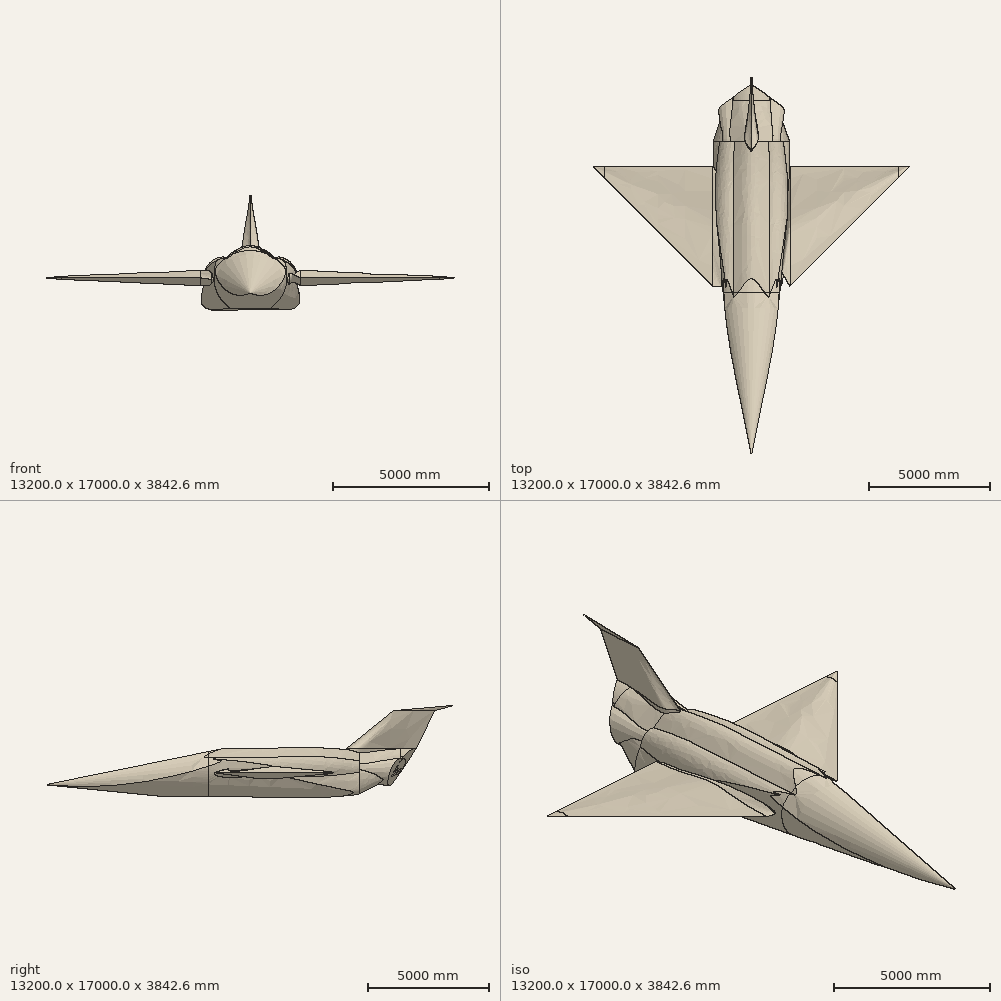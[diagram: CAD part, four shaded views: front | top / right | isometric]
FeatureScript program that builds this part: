
annotation { "Feature Type Name" : "Feature", "Feature Type Description" : "" }
export const myFeature = defineFeature(function(context is Context, id is Id, definition is map)
    precondition{}
    {
        {
            var Q0;
            Q0=qCreatedBy(makeId("Front.planeOp"),FACE);
            cPlane(context, id + "F0", {"entities" : qUnion([Q0]), "cplaneType" : CPlaneType.OFFSET, "offset" : 1750 * mm, "width" : 152.4 * mm, "height" : 152.4 * mm});
        }
        {
            var Q0;
            Q0=qCreatedBy(id+"F0.planeOp",FACE);
            var sketch = newSketch(context, id + "F1", { "sketchPlane" : qUnion([Q0])});
            skLineSegment(sketch, "E0.top", {"start": v(-1394.2, -1000) * mm, "end": v(1394.2, -1000) * mm});
            skPoint(sketch, "E0.middle", {"position": v(0, 0) * mm});
            skFitSpline(sketch, "E1", {"points": [v(-1600, -1000) * mm, v(-848, 530) * mm, v(0, 1000) * mm, v(848, 530) * mm, v(1600, -1000) * mm], "startDerivative": vector(0, 10524.75) * mm, "endDerivative": vector(0, -10524.75) * mm});
            skArc(sketch, "E2", {"start": v(-735.27, 618.52) * mm, "mid": v(-1273.27, 435.52) * mm, "end": v(-1440.68, -107.53) * mm});
            skArc(sketch, "E3.trimOffspring", {"start": v(1440.68, -107.53) * mm, "mid": v(1273.27, 435.52) * mm, "end": v(735.27, 618.52) * mm});
            skFitSpline(sketch, "E4.trimOffspring", {"points": [v(-1600, -1000) * mm, v(-848, 530) * mm, v(0, 1000) * mm, v(848, 530) * mm, v(1600, -1000) * mm], "startDerivative": vector(0, 10524.75) * mm, "endDerivative": vector(0, -10524.75) * mm});
            skFitSpline(sketch, "E5.trimOffspring", {"points": [v(-1600, -1000) * mm, v(-848, 530) * mm, v(0, 1000) * mm, v(848, 530) * mm, v(1600, -1000) * mm], "startDerivative": vector(0, 10524.75) * mm, "endDerivative": vector(0, -10524.75) * mm});
            skArc(sketch, "E6.filletArc", {"start": v(-1593.82, -787.83) * mm, "mid": v(-1539.85, -937.05) * mm, "end": v(-1394.2, -1000) * mm});
            skArc(sketch, "E7.filletArc", {"start": v(1394.2, -1000) * mm, "mid": v(1539.85, -937.05) * mm, "end": v(1593.82, -787.83) * mm});
            skSolve(sketch);
        }
        {
            var Q0;
            Q0=qCreatedBy(makeId("Front.planeOp"),FACE);
            var sketch = newSketch(context, id + "F2", { "sketchPlane" : qUnion([Q0])});
            skLineSegment(sketch, "E8.top", {"start": v(-1394.2, -1000) * mm, "end": v(1394.2, -1000) * mm});
            skPoint(sketch, "E8.middle", {"position": v(0, 0) * mm});
            skFitSpline(sketch, "E9", {"points": [v(-1600, -1000) * mm, v(-848, 530) * mm, v(0, 1000) * mm, v(848, 530) * mm, v(1600, -1000) * mm], "startDerivative": vector(0, 10524.75) * mm, "endDerivative": vector(0, -10524.75) * mm});
            skArc(sketch, "E10", {"start": v(-735.27, 618.52) * mm, "mid": v(-1273.27, 435.52) * mm, "end": v(-1440.68, -107.53) * mm});
            skArc(sketch, "E11.trimOffspring", {"start": v(1440.68, -107.53) * mm, "mid": v(1273.27, 435.52) * mm, "end": v(735.27, 618.52) * mm});
            skFitSpline(sketch, "E12.trimOffspring", {"points": [v(-1600, -1000) * mm, v(-848, 530) * mm, v(0, 1000) * mm, v(848, 530) * mm, v(1600, -1000) * mm], "startDerivative": vector(0, 10524.75) * mm, "endDerivative": vector(0, -10524.75) * mm});
            skFitSpline(sketch, "E13.trimOffspring", {"points": [v(-1600, -1000) * mm, v(-848, 530) * mm, v(0, 1000) * mm, v(848, 530) * mm, v(1600, -1000) * mm], "startDerivative": vector(0, 10524.75) * mm, "endDerivative": vector(0, -10524.75) * mm});
            skArc(sketch, "E14.filletArc", {"start": v(-1593.82, -787.83) * mm, "mid": v(-1539.85, -937.05) * mm, "end": v(-1394.2, -1000) * mm});
            skArc(sketch, "E15.filletArc", {"start": v(1394.2, -1000) * mm, "mid": v(1539.85, -937.05) * mm, "end": v(1593.82, -787.83) * mm});
            skSolve(sketch);
        }
        {
            var Q0;
            Q0=qCreatedBy(makeId("Front.planeOp"),FACE);
            cPlane(context, id + "F3", {"entities" : qUnion([Q0]), "cplaneType" : CPlaneType.OFFSET, "offset" : 3500 * mm, "oppositeDirection" : true, "width" : 150 * mm, "height" : 150 * mm});
        }
        {
            var Q0;
            Q0=qCreatedBy(id+"F3.planeOp",FACE);
            var sketch = newSketch(context, id + "F4", { "sketchPlane" : qUnion([Q0])});
            skLineSegment(sketch, "E16.top", {"start": v(-1394.2, -1000) * mm, "end": v(1394.2, -1000) * mm});
            skPoint(sketch, "E16.middle", {"position": v(0, 0) * mm});
            skFitSpline(sketch, "E17", {"points": [v(-1600, -1000) * mm, v(-848, 530) * mm, v(0, 1000) * mm, v(848, 530) * mm, v(1600, -1000) * mm], "startDerivative": vector(0, 10524.75) * mm, "endDerivative": vector(0, -10524.75) * mm});
            skArc(sketch, "E18", {"start": v(-735.27, 618.52) * mm, "mid": v(-1273.27, 435.52) * mm, "end": v(-1440.68, -107.53) * mm});
            skArc(sketch, "E19.trimOffspring", {"start": v(1440.68, -107.53) * mm, "mid": v(1273.27, 435.52) * mm, "end": v(735.27, 618.52) * mm});
            skFitSpline(sketch, "E20.trimOffspring", {"points": [v(-1600, -1000) * mm, v(-848, 530) * mm, v(0, 1000) * mm, v(848, 530) * mm, v(1600, -1000) * mm], "startDerivative": vector(0, 10524.75) * mm, "endDerivative": vector(0, -10524.75) * mm});
            skFitSpline(sketch, "E21.trimOffspring", {"points": [v(-1600, -1000) * mm, v(-848, 530) * mm, v(0, 1000) * mm, v(848, 530) * mm, v(1600, -1000) * mm], "startDerivative": vector(0, 10524.75) * mm, "endDerivative": vector(0, -10524.75) * mm});
            skArc(sketch, "E22.filletArc", {"start": v(-1593.82, -787.83) * mm, "mid": v(-1539.85, -937.05) * mm, "end": v(-1394.2, -1000) * mm});
            skArc(sketch, "E23.filletArc", {"start": v(1394.2, -1000) * mm, "mid": v(1539.85, -937.05) * mm, "end": v(1593.82, -787.83) * mm});
            skSolve(sketch);
        }
        {
            var Q0;
            Q0=qCreatedBy(makeId("Front.planeOp"),FACE);
            cPlane(context, id + "F5", {"entities" : qUnion([Q0]), "cplaneType" : CPlaneType.OFFSET, "offset" : 4500 * mm, "oppositeDirection" : true, "width" : 150 * mm, "height" : 150 * mm});
        }
        {
            var Q0;
            Q0=qCreatedBy(id+"F5.planeOp",FACE);
            var sketch = newSketch(context, id + "F6", { "sketchPlane" : qUnion([Q0])});
            skLineSegment(sketch, "E24.top", {"start": v(-1413.07, -900) * mm, "end": v(1413.07, -900) * mm});
            skPoint(sketch, "E24.middle", {"position": v(0, 0) * mm});
            skFitSpline(sketch, "E25", {"points": [v(-1600, -900) * mm, v(-784.42, 441.24) * mm, v(0, 900) * mm, v(784.42, 441.24) * mm, v(1600, -900) * mm], "startDerivative": vector(0, 9508.62) * mm, "endDerivative": vector(0, -9508.62) * mm});
            skArc(sketch, "E26", {"start": v(-719.25, 488.69) * mm, "mid": v(-1131.76, 394.84) * mm, "end": v(-1324.66, 18.33) * mm});
            skArc(sketch, "E27.trimOffspring", {"start": v(1324.66, 18.33) * mm, "mid": v(1131.76, 394.84) * mm, "end": v(719.25, 488.69) * mm});
            skFitSpline(sketch, "E28.trimOffspring", {"points": [v(-1600, -900) * mm, v(-784.42, 441.24) * mm, v(0, 900) * mm, v(784.42, 441.24) * mm, v(1600, -900) * mm], "startDerivative": vector(0, 9508.62) * mm, "endDerivative": vector(0, -9508.62) * mm});
            skFitSpline(sketch, "E29.trimOffspring", {"points": [v(-1600, -900) * mm, v(-784.42, 441.24) * mm, v(0, 900) * mm, v(784.42, 441.24) * mm, v(1600, -900) * mm], "startDerivative": vector(0, 9508.62) * mm, "endDerivative": vector(0, -9508.62) * mm});
            skArc(sketch, "E30.filletArc", {"start": v(-1592.48, -705.43) * mm, "mid": v(-1545.4, -842.02) * mm, "end": v(-1413.07, -900) * mm});
            skArc(sketch, "E31.filletArc", {"start": v(1413.07, -900) * mm, "mid": v(1545.4, -842.02) * mm, "end": v(1592.48, -705.43) * mm});
            skLineSegment(sketch, "E32", {"start": v(-719.25, 488.69) * mm, "end": v(-1324.66, 18.33) * mm, "construction": true});
            skLineSegment(sketch, "E33", {"start": v(719.25, 488.69) * mm, "end": v(1324.66, 18.33) * mm, "construction": true});
            skSolve(sketch);
        }
        {
            var Q0;
            Q0=qCreatedBy(makeId("Front.planeOp"),FACE);
            cPlane(context, id + "F7", {"entities" : qUnion([Q0]), "cplaneType" : CPlaneType.OFFSET, "offset" : 6232.05 * mm, "oppositeDirection" : true, "width" : 150 * mm, "height" : 150 * mm});
        }
        {
            var Q0;
            Q0=qCreatedBy(id+"F7.planeOp",FACE);
            var sketch = newSketch(context, id + "F8", { "sketchPlane" : qUnion([Q0])});
            skArc(sketch, "E34", {"start": v(998.61, 52.63) * mm, "mid": v(0, 1000) * mm, "end": v(-998.61, 52.63) * mm});
            skLineSegment(sketch, "E35", {"start": v(0, 0) * mm, "end": v(-948.68, 0) * mm});
            skLineSegment(sketch, "E36", {"start": v(0, 0) * mm, "end": v(948.68, 0) * mm});
            skPoint(sketch, "E37.visualSharp", {"position": v(-1000, 0) * mm});
            skArc(sketch, "E37.filletArc", {"start": v(-998.61, 52.63) * mm, "mid": v(-984.96, 15.59) * mm, "end": v(-948.68, 0) * mm});
            skPoint(sketch, "E38.visualSharp", {"position": v(1000, 0) * mm});
            skArc(sketch, "E38.filletArc", {"start": v(948.68, 0) * mm, "mid": v(984.96, 15.59) * mm, "end": v(998.61, 52.63) * mm});
            skLineSegment(sketch, "E39", {"start": v(0, 1000) * mm, "end": v(0, 675) * mm, "construction": true});
            skPoint(sketch, "E39.endSnap0", {"position": v(0, 1000) * mm});
            skLineSegment(sketch, "E40", {"start": v(0, 675) * mm, "end": v(737.82, 675) * mm, "construction": true});
            skLineSegment(sketch, "E41", {"start": v(0, 675) * mm, "end": v(-737.82, 675) * mm, "construction": true});
            skSolve(sketch);
        }
        {
            var Q0;
            Q0=qSketchRegion(id+"F1",true);
            var Q1;
            Q1=qSketchRegion(id+"F2",true);
            var Q2;
            Q2=qSketchRegion(id+"F4",true);
            var Q3;
            Q3=qSketchRegion(id+"F6",true);
            loft(context, id + "F9", {"sheetProfilesArray" : [{ "sheetProfileEntities" : qUnion([Q0]) }, { "sheetProfileEntities" : qUnion([Q1]) }, { "sheetProfileEntities" : qUnion([Q2]) }, { "sheetProfileEntities" : qUnion([Q3]) }]});
        }
        {
            var Q0;
            Q0=sQuery(id+"F6.wireOp",EDGE,"E32");
            var Q1;
            Q1=sQuery(id+"F8.wireOp",VERTEX,"E41.end");
            cPlane(context, id + "F10", {"entities" : qUnion([Q0, Q1]), "cplaneType" : CPlaneType.LINE_ANGLE, "offset" : 25 * mm, "angle" : 0 * degree, "width" : 150 * mm, "height" : 150 * mm});
        }
        {
            var Q0;
            Q0=qCreatedBy(id+"F10.planeOp",FACE);
            var sketch = newSketch(context, id + "F11", { "sketchPlane" : qUnion([Q0])});
            skLineSegment(sketch, "E42", {"start": v(-589.34, -4526.34) * mm, "end": v(-612.8, -6268.32) * mm});
            skLineSegment(sketch, "E43", {"start": v(-1354.08, -4472.19) * mm, "end": v(-612.8, -6268.32) * mm});
            skSolve(sketch);
        }
        {
            var Q0;
            Q0=sQuery(id+"F6.wireOp",EDGE,"E33");
            var Q1;
            Q1=sQuery(id+"F8.wireOp",VERTEX,"E40.end");
            cPlane(context, id + "F12", {"entities" : qUnion([Q0, Q1]), "cplaneType" : CPlaneType.LINE_ANGLE, "offset" : 25 * mm, "angle" : 0 * degree, "width" : 150 * mm, "height" : 150 * mm});
        }
        {
            var Q0;
            Q0=qCreatedBy(id+"F12.planeOp",FACE);
            var sketch = newSketch(context, id + "F13", { "sketchPlane" : qUnion([Q0])});
            skLineSegment(sketch, "E44", {"start": v(589.34, 4526.34) * mm, "end": v(612.8, 6268.32) * mm});
            skLineSegment(sketch, "E45", {"start": v(1354.08, 4472.19) * mm, "end": v(612.8, 6268.32) * mm});
            skSolve(sketch);
        }
        {
            var Q1;
            Q1=makeQuery(id+"F6.imprint","IMPRINT",FACE,{"disambiguationData":[TD([[makeQuery(id+"F6.imprint","IMPRINT",EDGE,{"derivedFrom":sQuery(id+"F6.wireOp",EDGE,"E24.top")}),1.0]])]});
            var Q2;
            Q2=makeQuery(id+"F8.imprint","IMPRINT",FACE,{"disambiguationData":[TD([[makeQuery(id+"F8.imprint","IMPRINT",EDGE,{"derivedFrom":sQuery(id+"F8.wireOp",EDGE,"E34")}),1.0]])]});
            var Q3;
            Q3=sQuery(id+"F11.wireOp",EDGE,"E42");
            var Q4;
            Q4=sQuery(id+"F13.wireOp",EDGE,"E44");
            loft(context, id + "F14", {"operationType" : NewBodyOperationType.ADD, "addGuides" : true, "sheetProfilesArray" : [{ "sheetProfileEntities" : qUnion([Q1]) }, { "sheetProfileEntities" : qUnion([Q2]) }], "guidesArray" : [{ "guideEntities" : qUnion([Q3]), "guideDerivativeType" : LoftGuideDerivativeType.DEFAULT, "guideDerivativeMagnitude" : 1 }, { "guideEntities" : qUnion([Q4]), "guideDerivativeType" : LoftGuideDerivativeType.DEFAULT, "guideDerivativeMagnitude" : 1 }]});
        }
        {
            var Q0;
            Q0=makeQuery(id+"F14.opLoft","CAP_FACE",FACE,{"disambiguationData":[OSD([makeQuery(id+"F8.imprint","IMPRINT",FACE,{"disambiguationData":[TD([[makeQuery(id+"F8.imprint","IMPRINT",EDGE,{"derivedFrom":sQuery(id+"F8.wireOp",EDGE,"E34")}),1.0]])]})])],"isStart":true});
            extrude(context, id + "F15", {"entities" : qUnion([Q0]), "operationType" : NewBodyOperationType.ADD, "depth" : 649.4 * mm});
        }
        {
            var Q0;
            Q0=qCreatedBy(makeId("Right.planeOp"),FACE);
            var sketch = newSketch(context, id + "F16", { "sketchPlane" : qUnion([Q0])});
            skLineSegment(sketch, "E46", {"start": v(0, 0) * mm, "end": v(4500, 0) * mm});
            skLineSegment(sketch, "E47", {"start": v(4500, 0) * mm, "end": v(6232.05, 0) * mm});
            skLineSegment(sketch, "E48", {"start": v(4500, 0) * mm, "end": v(4500, 1000) * mm});
            skLineSegment(sketch, "E49", {"start": v(4500, 1000) * mm, "end": v(6881.46, 1000) * mm});
            skLineSegment(sketch, "E50", {"start": v(6881.46, 1000) * mm, "end": v(6881.46, -1000) * mm});
            skLineSegment(sketch, "E51", {"start": v(6881.46, 1000) * mm, "end": v(6232.05, 0) * mm});
            skLineSegment(sketch, "E52", {"start": v(6232.05, 0) * mm, "end": v(5582.64, -1000) * mm});
            skLineSegment(sketch, "E53", {"start": v(5582.64, -1000) * mm, "end": v(6881.46, -1000) * mm});
            skSolve(sketch);
        }
        {
            var Q0;
            Q0=makeQuery(id+"F16.imprint","IMPRINT",FACE,{"disambiguationData":[TD([[makeQuery(id+"F16.imprint","IMPRINT",EDGE,{"derivedFrom":sQuery(id+"F16.wireOp",EDGE,"E50")}),-1.0]])]});
            var Q1;
            Q1=sQuery(id+"F16.wireOp",EDGE,"E49");
            revolve(context, id + "F17", {"operationType" : NewBodyOperationType.REMOVE, "entities" : qUnion([Q0]), "axis" : qUnion([Q1]), "revolveType" : RevolveType.SYMMETRIC, "oppositeDirection" : true, "angle" : 182 * degree});
        }
        {
            var Q0;
            Q0=makeQuery(id+"F9.opLoft","CAP_FACE",FACE,{"disambiguationData":[OSD([makeQuery(id+"F1.imprint","IMPRINT",FACE,{"disambiguationData":[TD([[makeQuery(id+"F1.imprint","IMPRINT",EDGE,{"derivedFrom":sQuery(id+"F1.wireOp",EDGE,"E0.top")}),1.0]])]})])],"isStart":true});
            extrude(context, id + "F18", {"entities" : qUnion([Q0]), "depth" : 6750 * mm});
        }
        {
            var Q0;
            Q0=qCreatedBy(makeId("Right.planeOp"),FACE);
            var sketch = newSketch(context, id + "F19", { "sketchPlane" : qUnion([Q0])});
            skLineSegment(sketch, "E54", {"start": v(0, 0) * mm, "end": v(-3500, 0) * mm});
            skLineSegment(sketch, "E55", {"start": v(-3500, 0) * mm, "end": v(-3500, -1000) * mm});
            skLineSegment(sketch, "E56", {"start": v(-3500, -1000) * mm, "end": v(-8500, -1000) * mm});
            skLineSegment(sketch, "E57", {"start": v(-8500, -1000) * mm, "end": v(-8500, -499.31) * mm});
            skLineSegment(sketch, "E58", {"start": v(-1151.4, 0) * mm, "end": v(-1151.4, 1000) * mm});
            skLineSegment(sketch, "E59", {"start": v(-1151.4, 1000) * mm, "end": v(-8500, -499.31) * mm});
            skLineSegment(sketch, "E60", {"start": v(-8500, -499.31) * mm, "end": v(-3500, -1000) * mm});
            skLineSegment(sketch, "E61", {"start": v(-1151.4, 1000) * mm, "end": v(-8500, 1000) * mm});
            skLineSegment(sketch, "E62", {"start": v(-8500, 1000) * mm, "end": v(-8500, -499.31) * mm});
            skLineSegment(sketch, "E63", {"start": v(-8500, -1000) * mm, "end": v(-8500, -1980) * mm});
            skLineSegment(sketch, "E64", {"start": v(-3500, -1000) * mm, "end": v(6286.5, -1980) * mm});
            skLineSegment(sketch, "E65", {"start": v(6286.5, -1980) * mm, "end": v(-8500, -1980) * mm});
            skLineSegment(sketch, "E66", {"start": v(-8500, -499.31) * mm, "end": v(-3500, -499.31) * mm});
            skSolve(sketch);
        }
        {
            var Q0;
            Q0=makeQuery(id+"F19.imprint","IMPRINT",FACE,{"disambiguationData":[TD([[makeQuery(id+"F19.imprint","IMPRINT",EDGE,{"derivedFrom":sQuery(id+"F19.wireOp",EDGE,"E59")}),-1.0]])]});
            var Q1;
            Q1=sQuery(id+"F19.wireOp",EDGE,"E66");
            revolve(context, id + "F20", {"operationType" : NewBodyOperationType.REMOVE, "entities" : qUnion([Q0]), "axis" : qUnion([Q1]), "revolveType" : RevolveType.SYMMETRIC, "oppositeDirection" : true, "angle" : 250 * degree});
        }
        {
            var Q0;
            Q0=makeQuery(id+"F19.imprint","IMPRINT",FACE,{"disambiguationData":[TD([[makeQuery(id+"F19.imprint","IMPRINT",EDGE,{"derivedFrom":sQuery(id+"F19.wireOp",EDGE,"E56")}),-1.0]])]});
            var Q1;
            Q1=makeQuery(id+"F19.imprint","IMPRINT",FACE,{"disambiguationData":[TD([[makeQuery(id+"F19.imprint","IMPRINT",EDGE,{"derivedFrom":sQuery(id+"F19.wireOp",EDGE,"E56")}),1.0]])]});
            var Q2;
            Q2=sQuery(id+"F19.wireOp",EDGE,"E54");
            revolve(context, id + "F21", {"operationType" : NewBodyOperationType.REMOVE, "entities" : qUnion([Q0, Q1]), "axis" : qUnion([Q2]), "revolveType" : RevolveType.SYMMETRIC, "oppositeDirection" : true, "angle" : 240 * degree});
        }
        {
            var Q0;
            Q0=qCreatedBy(makeId("Front.planeOp"),FACE);
            cPlane(context, id + "F22", {"entities" : qUnion([Q0]), "cplaneType" : CPlaneType.OFFSET, "offset" : 3500 * mm, "oppositeDirection" : true, "width" : 150 * mm, "height" : 150 * mm});
        }
        {
            var Q0;
            Q0=qCreatedBy(id+"F22.planeOp",FACE);
            var sketch = newSketch(context, id + "F23", { "sketchPlane" : qUnion([Q0])});
            skCircle(sketch, "E67", {"center": v(-825, 0) * mm, "radius": 600 * mm});
            skCircle(sketch, "E68", {"center": v(825, 0) * mm, "radius": 600 * mm});
            skSolve(sketch);
        }
        {
            var Q0;
            Q0=qCreatedBy(makeId("Front.planeOp"),FACE);
            cPlane(context, id + "F24", {"entities" : qUnion([Q0]), "cplaneType" : CPlaneType.OFFSET, "offset" : 4500 * mm, "oppositeDirection" : true, "width" : 150 * mm, "height" : 150 * mm});
        }
        {
            var Q0;
            Q0=qCreatedBy(id+"F24.planeOp",FACE);
            var sketch = newSketch(context, id + "F25", { "sketchPlane" : qUnion([Q0])});
            skCircle(sketch, "E69", {"center": v(-825, 0) * mm, "radius": 400 * mm});
            skCircle(sketch, "E70", {"center": v(825, 0) * mm, "radius": 400 * mm});
            skSolve(sketch);
        }
        {
            var Q0;
            Q0=qCreatedBy(makeId("Front.planeOp"),FACE);
            cPlane(context, id + "F26", {"entities" : qUnion([Q0]), "cplaneType" : CPlaneType.OFFSET, "offset" : 6232.05 * mm, "oppositeDirection" : true, "width" : 150 * mm, "height" : 150 * mm});
        }
        {
            var Q0;
            Q0=qCreatedBy(id+"F26.planeOp",FACE);
            var sketch = newSketch(context, id + "F27", { "sketchPlane" : qUnion([Q0])});
            skCircle(sketch, "E71", {"center": v(-825, 0) * mm, "radius": 600 * mm});
            skCircle(sketch, "E72", {"center": v(825, 0) * mm, "radius": 600 * mm});
            skSolve(sketch);
        }
        {
            var Q0;
            Q0=qCreatedBy(makeId("Front.planeOp"),FACE);
            cPlane(context, id + "F28", {"entities" : qUnion([Q0]), "cplaneType" : CPlaneType.OFFSET, "offset" : 6732.05 * mm, "oppositeDirection" : true, "width" : 150 * mm, "height" : 150 * mm});
        }
        {
            var Q0;
            Q0=qCreatedBy(id+"F28.planeOp",FACE);
            var sketch = newSketch(context, id + "F29", { "sketchPlane" : qUnion([Q0])});
            skCircle(sketch, "E73", {"center": v(-825, 0) * mm, "radius": 600 * mm});
            skCircle(sketch, "E74", {"center": v(825, 0) * mm, "radius": 600 * mm});
            skSolve(sketch);
        }
        {
            var Q0;
            Q0=makeQuery(id+"F23.imprint","IMPRINT",FACE,{"disambiguationData":[TD([[makeQuery(id+"F23.imprint","IMPRINT",EDGE,{"derivedFrom":sQuery(id+"F23.wireOp",EDGE,"E67")}),1.0]])]});
            var Q1;
            Q1=makeQuery(id+"F25.imprint","IMPRINT",FACE,{"disambiguationData":[TD([[makeQuery(id+"F25.imprint","IMPRINT",EDGE,{"derivedFrom":sQuery(id+"F25.wireOp",EDGE,"E69")}),1.0]])]});
            var Q2;
            Q2=makeQuery(id+"F27.imprint","IMPRINT",FACE,{"disambiguationData":[TD([[makeQuery(id+"F27.imprint","IMPRINT",EDGE,{"derivedFrom":sQuery(id+"F27.wireOp",EDGE,"E71")}),1.0]])]});
            var Q3;
            Q3=makeQuery(id+"F29.imprint","IMPRINT",FACE,{"disambiguationData":[TD([[makeQuery(id+"F29.imprint","IMPRINT",EDGE,{"derivedFrom":sQuery(id+"F29.wireOp",EDGE,"E73")}),1.0]])]});
            loft(context, id + "F30", {"sheetProfilesArray" : [{ "sheetProfileEntities" : qUnion([Q0]) }, { "sheetProfileEntities" : qUnion([Q1]) }, { "sheetProfileEntities" : qUnion([Q2]) }, { "sheetProfileEntities" : qUnion([Q3]) }]});
        }
        {
            var Q0;
            Q0=makeQuery(id+"F23.imprint","IMPRINT",FACE,{"disambiguationData":[TD([[makeQuery(id+"F23.imprint","IMPRINT",EDGE,{"derivedFrom":sQuery(id+"F23.wireOp",EDGE,"E68")}),1.0]])]});
            var Q1;
            Q1=makeQuery(id+"F25.imprint","IMPRINT",FACE,{"disambiguationData":[TD([[makeQuery(id+"F25.imprint","IMPRINT",EDGE,{"derivedFrom":sQuery(id+"F25.wireOp",EDGE,"E70")}),1.0]])]});
            var Q2;
            Q2=makeQuery(id+"F27.imprint","IMPRINT",FACE,{"disambiguationData":[TD([[makeQuery(id+"F27.imprint","IMPRINT",EDGE,{"derivedFrom":sQuery(id+"F27.wireOp",EDGE,"E72")}),1.0]])]});
            var Q3;
            Q3=makeQuery(id+"F29.imprint","IMPRINT",FACE,{"disambiguationData":[TD([[makeQuery(id+"F29.imprint","IMPRINT",EDGE,{"derivedFrom":sQuery(id+"F29.wireOp",EDGE,"E74")}),1.0]])]});
            loft(context, id + "F31", {"sheetProfilesArray" : [{ "sheetProfileEntities" : qUnion([Q0]) }, { "sheetProfileEntities" : qUnion([Q1]) }, { "sheetProfileEntities" : qUnion([Q2]) }, { "sheetProfileEntities" : qUnion([Q3]) }]});
        }
        {
            var Q0;
            Q0=qCreatedBy(makeId("Top.planeOp"),FACE);
            var sketch = newSketch(context, id + "F32", { "sketchPlane" : qUnion([Q0])});
            skLineSegment(sketch, "E75", {"start": v(0, 0) * mm, "end": v(0, 1000) * mm});
            skLineSegment(sketch, "E76", {"start": v(0, 1000) * mm, "end": v(-1600, 1000) * mm});
            skLineSegment(sketch, "E77", {"start": v(-1600, 1000) * mm, "end": v(-1600, -1500) * mm});
            skLineSegment(sketch, "E78", {"start": v(-1600, 1000) * mm, "end": v(-1600, 3500) * mm});
            skLineSegment(sketch, "E79", {"start": v(-1600, 3500) * mm, "end": v(-6100, 3500) * mm});
            skLineSegment(sketch, "E80", {"start": v(-6100, 3500) * mm, "end": v(-6600, 3500) * mm});
            skLineSegment(sketch, "E81", {"start": v(-6100, 3500) * mm, "end": v(-6100, 3000) * mm});
            skLineSegment(sketch, "E82", {"start": v(-1600, -1500) * mm, "end": v(-6100, 3000) * mm});
            skLineSegment(sketch, "E83", {"start": v(0, 1000) * mm, "end": v(1600, 1000) * mm});
            skLineSegment(sketch, "E84", {"start": v(1600, 1000) * mm, "end": v(1600, -1500) * mm});
            skLineSegment(sketch, "E85", {"start": v(1600, 1000) * mm, "end": v(1600, 3500) * mm});
            skLineSegment(sketch, "E86", {"start": v(1600, 3500) * mm, "end": v(6100, 3500) * mm});
            skLineSegment(sketch, "E87", {"start": v(6100, 3500) * mm, "end": v(6600, 3500) * mm});
            skLineSegment(sketch, "E88", {"start": v(6100, 3500) * mm, "end": v(6100, 3000) * mm});
            skLineSegment(sketch, "E89", {"start": v(1600, -1500) * mm, "end": v(6100, 3000) * mm});
            skSolve(sketch);
        }
        {
            var Q0;
            Q0=qCreatedBy(makeId("Right.planeOp"),FACE);
            var sketch = newSketch(context, id + "F33", { "sketchPlane" : qUnion([Q0])});
            skFitSpline(sketch, "E90", {"points": [v(-1500, -50) * mm, v(0, 250) * mm, v(3000, -50) * mm, v(0, -250) * mm, v(-1500, -50) * mm]});
            skSolve(sketch);
        }
        {
            var Q0;
            Q0=qCreatedBy(makeId("Right.planeOp"),FACE);
            cPlane(context, id + "F34", {"entities" : qUnion([Q0]), "cplaneType" : CPlaneType.OFFSET, "offset" : 1600 * mm, "oppositeDirection" : true, "width" : 150 * mm, "height" : 150 * mm});
        }
        {
            var Q0;
            Q0=qCreatedBy(id+"F34.planeOp",FACE);
            var sketch = newSketch(context, id + "F35", { "sketchPlane" : qUnion([Q0])});
            skFitSpline(sketch, "E91", {"points": [v(-1500, 0) * mm, v(1000, 250) * mm, v(3500, 0) * mm], "startDerivative": vector(7500, 0) * mm, "endDerivative": vector(7500, 0) * mm});
            skFitSpline(sketch, "E92", {"points": [v(-1500, 0) * mm, v(1000, -250) * mm, v(3500, 0) * mm], "startDerivative": vector(5000, -750) * mm, "endDerivative": vector(7500, 0) * mm});
            skSolve(sketch);
        }
        {
            var Q0;
            Q0=qCreatedBy(makeId("Right.planeOp"),FACE);
            cPlane(context, id + "F36", {"entities" : qUnion([Q0]), "cplaneType" : CPlaneType.OFFSET, "offset" : 1600 * mm, "width" : 150 * mm, "height" : 150 * mm});
        }
        {
            var Q0;
            Q0=qCreatedBy(id+"F36.planeOp",FACE);
            var sketch = newSketch(context, id + "F37", { "sketchPlane" : qUnion([Q0])});
            skFitSpline(sketch, "E93", {"points": [v(-1500, 0) * mm, v(1000, 250) * mm, v(3500, 0) * mm], "startDerivative": vector(7500, 0) * mm, "endDerivative": vector(7500, 0) * mm});
            skFitSpline(sketch, "E94", {"points": [v(-1500, 0) * mm, v(1000, -250) * mm, v(3500, 0) * mm], "startDerivative": vector(5000, -750) * mm, "endDerivative": vector(7500, 0) * mm});
            skSolve(sketch);
        }
        {
            var Q0;
            Q0=qCreatedBy(makeId("Right.planeOp"),FACE);
            cPlane(context, id + "F38", {"entities" : qUnion([Q0]), "cplaneType" : CPlaneType.OFFSET, "offset" : 6100 * mm, "oppositeDirection" : true, "width" : 150 * mm, "height" : 150 * mm});
        }
        {
            var Q0;
            Q0=qCreatedBy(id+"F38.planeOp",FACE);
            var sketch = newSketch(context, id + "F39", { "sketchPlane" : qUnion([Q0])});
            skFitSpline(sketch, "E95", {"points": [v(3000, 0) * mm, v(3250, 50) * mm, v(3500, 0) * mm], "startDerivative": vector(750, 0) * mm, "endDerivative": vector(750, 0) * mm});
            skFitSpline(sketch, "E96", {"points": [v(3000, 0) * mm, v(3250, -50) * mm, v(3500, 0) * mm], "startDerivative": vector(500, -150) * mm, "endDerivative": vector(750, 0) * mm});
            skSolve(sketch);
        }
        {
            var Q0;
            Q0=qCreatedBy(makeId("Right.planeOp"),FACE);
            cPlane(context, id + "F40", {"entities" : qUnion([Q0]), "cplaneType" : CPlaneType.OFFSET, "offset" : 6100 * mm, "width" : 150 * mm, "height" : 150 * mm});
        }
        {
            var Q0;
            Q0=qCreatedBy(id+"F40.planeOp",FACE);
            var sketch = newSketch(context, id + "F41", { "sketchPlane" : qUnion([Q0])});
            skFitSpline(sketch, "E97", {"points": [v(3000, 0) * mm, v(3250, 50) * mm, v(3500, 0) * mm], "startDerivative": vector(850.99, 0) * mm, "endDerivative": vector(750, 0) * mm});
            skFitSpline(sketch, "E98", {"points": [v(3000, 0) * mm, v(3250, -50) * mm, v(3500, 0) * mm], "startDerivative": vector(500, -150) * mm, "endDerivative": vector(750, 0) * mm});
            skSolve(sketch);
        }
        {
            var Q0;
            Q0=qSketchRegion(id+"F33",true);
            extrude(context, id + "F42", {"entities" : qUnion([Q0]), "endBound" : BoundingType.SYMMETRIC, "depth" : 2500 * mm});
        }
        {
            var Q1;
            Q1=makeQuery(id+"F42.opExtrude","CAP_FACE",FACE,{"disambiguationData":[OSD([sQuery(id+"F33.wireOp",EDGE,"E90")])],"isStart":true});
            var Q2;
            {var subQ0=sQuery(id+"F35.wireOp",EDGE,"E91");Q2=makeQuery(id+"F35.imprint","IMPRINT",FACE,{"disambiguationData":[TD([[makeQuery(id+"F35.imprint","IMPRINT",EDGE,{"derivedFrom":subQ0}),-1.0]])]});}
            loft(context, id + "F43", {"operationType" : NewBodyOperationType.ADD, "sheetProfilesArray" : [{ "sheetProfileEntities" : qUnion([Q1]) }, { "sheetProfileEntities" : qUnion([Q2]) }]});
        }
        {
            var Q1;
            Q1=makeQuery(id+"F42.opExtrude","CAP_FACE",FACE,{"disambiguationData":[OSD([sQuery(id+"F33.wireOp",EDGE,"E90")])],"isStart":false});
            var Q2;
            {var subQ0=sQuery(id+"F37.wireOp",EDGE,"E93");Q2=makeQuery(id+"F37.imprint","IMPRINT",FACE,{"disambiguationData":[TD([[makeQuery(id+"F37.imprint","IMPRINT",EDGE,{"derivedFrom":subQ0}),-1.0]])]});}
            loft(context, id + "F44", {"operationType" : NewBodyOperationType.ADD, "sheetProfilesArray" : [{ "sheetProfileEntities" : qUnion([Q1]) }, { "sheetProfileEntities" : qUnion([Q2]) }]});
        }
        {
            var Q1;
            {var subQ0=sQuery(id+"F35.wireOp",EDGE,"E91");Q1=makeQuery(id+"F43.opLoft","CAP_FACE",FACE,{"disambiguationData":[OSD([makeQuery(id+"F35.imprint","IMPRINT",FACE,{"disambiguationData":[TD([[makeQuery(id+"F35.imprint","IMPRINT",EDGE,{"derivedFrom":subQ0}),-1.0]])]})])],"isStart":true});}
            var Q2;
            {var subQ0=sQuery(id+"F39.wireOp",EDGE,"E95");Q2=makeQuery(id+"F39.imprint","IMPRINT",FACE,{"disambiguationData":[TD([[makeQuery(id+"F39.imprint","IMPRINT",EDGE,{"derivedFrom":subQ0}),-1.0]])]});}
            loft(context, id + "F45", {"operationType" : NewBodyOperationType.ADD, "sheetProfilesArray" : [{ "sheetProfileEntities" : qUnion([Q1]) }, { "sheetProfileEntities" : qUnion([Q2]) }]});
        }
        {
            var Q1;
            {var subQ0=sQuery(id+"F37.wireOp",EDGE,"E93");Q1=makeQuery(id+"F44.opLoft","CAP_FACE",FACE,{"disambiguationData":[OSD([makeQuery(id+"F37.imprint","IMPRINT",FACE,{"disambiguationData":[TD([[makeQuery(id+"F37.imprint","IMPRINT",EDGE,{"derivedFrom":subQ0}),-1.0]])]})])],"isStart":true});}
            var Q2;
            {var subQ0=sQuery(id+"F41.wireOp",EDGE,"E97");Q2=makeQuery(id+"F41.imprint","IMPRINT",FACE,{"disambiguationData":[TD([[makeQuery(id+"F41.imprint","IMPRINT",EDGE,{"derivedFrom":subQ0}),-1.0]])]});}
            loft(context, id + "F46", {"operationType" : NewBodyOperationType.ADD, "sheetProfilesArray" : [{ "sheetProfileEntities" : qUnion([Q1]) }, { "sheetProfileEntities" : qUnion([Q2]) }]});
        }
        {
            var Q1;
            {var subQ0=sQuery(id+"F39.wireOp",EDGE,"E95");Q1=makeQuery(id+"F45.opLoft","CAP_FACE",FACE,{"disambiguationData":[OSD([makeQuery(id+"F39.imprint","IMPRINT",FACE,{"disambiguationData":[TD([[makeQuery(id+"F39.imprint","IMPRINT",EDGE,{"derivedFrom":subQ0}),-1.0]])]})])],"isStart":true});}
            var Q2;
            Q2=sQuery(id+"F32.wireOp",VERTEX,"E80.end");
            loft(context, id + "F47", {"operationType" : NewBodyOperationType.ADD, "sheetProfilesArray" : [{ "sheetProfileEntities" : qUnion([Q1]) }, { "sheetProfileEntities" : qUnion([Q2]) }]});
        }
        {
            var Q1;
            {var subQ0=sQuery(id+"F41.wireOp",EDGE,"E97");Q1=makeQuery(id+"F46.opLoft","CAP_FACE",FACE,{"disambiguationData":[OSD([makeQuery(id+"F41.imprint","IMPRINT",FACE,{"disambiguationData":[TD([[makeQuery(id+"F41.imprint","IMPRINT",EDGE,{"derivedFrom":subQ0}),-1.0]])]})])],"isStart":true});}
            var Q2;
            Q2=sQuery(id+"F32.wireOp",VERTEX,"E87.end");
            loft(context, id + "F48", {"operationType" : NewBodyOperationType.ADD, "sheetProfilesArray" : [{ "sheetProfileEntities" : qUnion([Q1]) }, { "sheetProfileEntities" : qUnion([Q2]) }]});
        }
        {
            var Q0;
            Q0=qCreatedBy(makeId("Right.planeOp"),FACE);
            var sketch = newSketch(context, id + "F49", { "sketchPlane" : qUnion([Q0])});
            skLineSegment(sketch, "E99", {"start": v(0, 0) * mm, "end": v(4500, 0) * mm});
            skLineSegment(sketch, "E100", {"start": v(4500, 0) * mm, "end": v(4500, 1000) * mm});
            skLineSegment(sketch, "E101", {"start": v(4500, 1000) * mm, "end": v(6881.46, 1000) * mm});
            skLineSegment(sketch, "E102", {"start": v(6881.46, 1000) * mm, "end": v(8500, 1000) * mm});
            skLineSegment(sketch, "E103", {"start": v(8500, 1000) * mm, "end": v(8500, 2800) * mm});
            skLineSegment(sketch, "E104", {"start": v(4500, 1000) * mm, "end": v(4000, 1000) * mm});
            skLineSegment(sketch, "E105", {"start": v(4500, 1000) * mm, "end": v(4500, 750) * mm});
            skLineSegment(sketch, "E106", {"start": v(4500, 750) * mm, "end": v(4000, 750) * mm});
            skLineSegment(sketch, "E107", {"start": v(4500, 750) * mm, "end": v(6250, 750) * mm});
            skLineSegment(sketch, "E108", {"start": v(4000, 1000) * mm, "end": v(5943.2, 2572.89) * mm});
            skLineSegment(sketch, "E109", {"start": v(6881.46, 1000) * mm, "end": v(7648.6, 2572.89) * mm});
            skLineSegment(sketch, "E110", {"start": v(5943.2, 2572.89) * mm, "end": v(7648.6, 2572.89) * mm});
            skSolve(sketch);
        }
        {
            var Q0;
            Q0=qCreatedBy(makeId("Top.planeOp"),FACE);
            cPlane(context, id + "F50", {"entities" : qUnion([Q0]), "cplaneType" : CPlaneType.OFFSET, "offset" : 750 * mm, "width" : 150 * mm, "height" : 150 * mm});
        }
        {
            var Q0;
            Q0=qCreatedBy(id+"F50.planeOp",FACE);
            var sketch = newSketch(context, id + "F51", { "sketchPlane" : qUnion([Q0])});
            skLineSegment(sketch, "E111", {"start": v(0, 4000) * mm, "end": v(0, 4500) * mm});
            skFitSpline(sketch, "E112", {"points": [v(0, 4000) * mm, v(-250, 4500) * mm, v(0, 6881.46) * mm], "startDerivative": vector(-952.81, 1209.5) * mm, "endDerivative": vector(754.5, 4205.42) * mm});
            skFitSpline(sketch, "E113", {"points": [v(0, 4000) * mm, v(250, 4500) * mm, v(0, 6881.46) * mm], "startDerivative": vector(952.81, 1209.5) * mm, "endDerivative": vector(-754.5, 4205.42) * mm});
            skSolve(sketch);
        }
        {
            var Q0;
            Q0=qCreatedBy(makeId("Top.planeOp"),FACE);
            cPlane(context, id + "F52", {"entities" : qUnion([Q0]), "cplaneType" : CPlaneType.OFFSET, "offset" : 1000 * mm, "width" : 150 * mm, "height" : 150 * mm});
        }
        {
            var Q0;
            Q0=qCreatedBy(id+"F52.planeOp",FACE);
            var sketch = newSketch(context, id + "F53", { "sketchPlane" : qUnion([Q0])});
            skFitSpline(sketch, "E114", {"points": [v(0, 4000) * mm, v(-250, 4500) * mm, v(0, 6881.46) * mm], "startDerivative": vector(0, 2302.24) * mm, "endDerivative": vector(0, 5298.17) * mm});
            skFitSpline(sketch, "E115", {"points": [v(0, 4000) * mm, v(250, 4500) * mm, v(0, 6881.46) * mm], "startDerivative": vector(0, 2302.24) * mm, "endDerivative": vector(0, 5298.17) * mm});
            skSolve(sketch);
        }
        {
            var Q0;
            Q0=qCreatedBy(makeId("Top.planeOp"),FACE);
            cPlane(context, id + "F54", {"entities" : qUnion([Q0]), "cplaneType" : CPlaneType.OFFSET, "offset" : 2572.89 * mm, "width" : 150 * mm, "height" : 150 * mm});
        }
        {
            var Q0;
            Q0=qCreatedBy(id+"F54.planeOp",FACE);
            var sketch = newSketch(context, id + "F55", { "sketchPlane" : qUnion([Q0])});
            skFitSpline(sketch, "E116", {"points": [v(0, 5943.2) * mm, v(-25, 6795.9) * mm, v(0, 7648.6) * mm], "startDerivative": vector(-75, 1705.4) * mm, "endDerivative": vector(75, 1705.4) * mm});
            skFitSpline(sketch, "E117", {"points": [v(0, 5943.2) * mm, v(25, 6795.9) * mm, v(0, 7648.6) * mm], "startDerivative": vector(75, 1705.4) * mm, "endDerivative": vector(-75, 1705.4) * mm});
            skSolve(sketch);
        }
        {
            var Q1;
            Q1=makeQuery(id+"F51.imprint","IMPRINT",FACE,{"disambiguationData":[TD([[makeQuery(id+"F51.imprint","IMPRINT",EDGE,{"derivedFrom":sQuery(id+"F51.wireOp",EDGE,"E112")}),-1.0]])]});
            var Q2;
            Q2 = qSketchRegion(id + "F53", true);
            loft(context, id + "F56", {"sheetProfilesArray" : [{ "sheetProfileEntities" : qUnion([Q1]) }, { "sheetProfileEntities" : qUnion([Q2]) }]});
        }
        {
            var Q1;
            {var subQ0=sQuery(id+"F53.wireOp",EDGE,"E114");Q1=makeQuery(id+"F56.opLoft","CAP_FACE",FACE,{"disambiguationData":[OSD([makeQuery(id+"F53.imprint","IMPRINT",FACE,{"disambiguationData":[TD([[makeQuery(id+"F53.imprint","IMPRINT",EDGE,{"derivedFrom":subQ0}),-1.0]])]})])],"isStart":true});}
            var Q2;
            Q2=makeQuery(id+"F55.imprint","IMPRINT",FACE,{"disambiguationData":[TD([[makeQuery(id+"F55.imprint","IMPRINT",EDGE,{"derivedFrom":sQuery(id+"F55.wireOp",EDGE,"E116")}),-1.0]])]});
            loft(context, id + "F57", {"operationType" : NewBodyOperationType.ADD, "sheetProfilesArray" : [{ "sheetProfileEntities" : qUnion([Q1]) }, { "sheetProfileEntities" : qUnion([Q2]) }]});
        }
        {
            var Q1;
            Q1=makeQuery(id+"F57.opLoft","CAP_FACE",FACE,{"disambiguationData":[OSD([makeQuery(id+"F55.imprint","IMPRINT",FACE,{"disambiguationData":[TD([[makeQuery(id+"F55.imprint","IMPRINT",EDGE,{"derivedFrom":sQuery(id+"F55.wireOp",EDGE,"E116")}),-1.0]])]})])],"isStart":true});
            var Q2;
            Q2=sQuery(id+"F49.wireOp",VERTEX,"E103.end");
            loft(context, id + "F58", {"operationType" : NewBodyOperationType.ADD, "sheetProfilesArray" : [{ "sheetProfileEntities" : qUnion([Q1]) }, { "sheetProfileEntities" : qUnion([Q2]) }]});
        }
        {
            var Q0;
            Q0=makeQuery(id+"F16.imprint","IMPRINT",FACE,{"disambiguationData":[TD([[makeQuery(id+"F16.imprint","IMPRINT",EDGE,{"derivedFrom":sQuery(id+"F16.wireOp",EDGE,"E50")}),-1.0]])]});
            var Q1;
            Q1=sQuery(id+"F16.wireOp",EDGE,"E49");
            revolve(context, id + "F59", {"operationType" : NewBodyOperationType.REMOVE, "entities" : qUnion([Q0]), "axis" : qUnion([Q1]), "revolveType" : RevolveType.SYMMETRIC, "oppositeDirection" : true, "angle" : 182 * degree});
        }
    });
